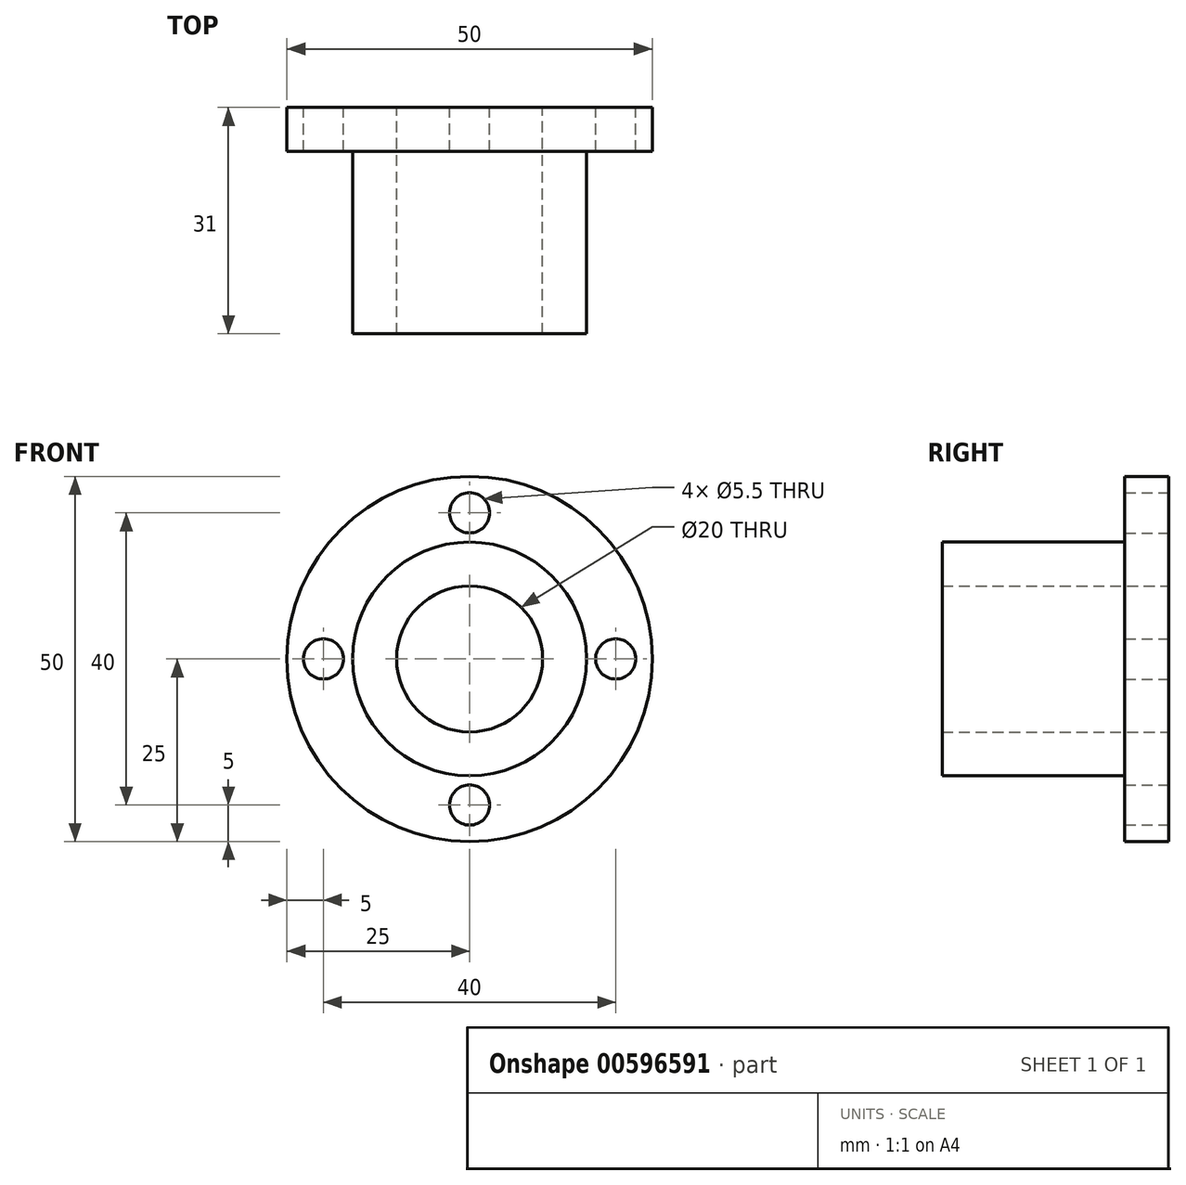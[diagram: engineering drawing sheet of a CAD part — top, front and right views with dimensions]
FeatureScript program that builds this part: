
annotation { "Feature Type Name" : "Feature", "Feature Type Description" : "" }
export const myFeature = defineFeature(function(context is Context, id is Id, definition is map)
    precondition{}
    {
        {
            var Q0;
            Q0=qCreatedBy(makeId("Front.planeOp"),FACE);
            var sketch = newSketch(context, id + "F0", { "sketchPlane" : qUnion([Q0])});
            skCircle(sketch, "E0", {"center": v(0, 0) * mm, "radius": 25 * mm});
            skSolve(sketch);
        }
        {
            var Q0;
            Q0 = qSketchRegion(id + "F0", true);
            extrude(context, id + "F1", {"entities" : qUnion([Q0]), "depth" : 6 * mm, "offsetDistance" : 25 * mm});
        }
        {
            var Q0;
            Q0=makeQuery(id+"F1.opExtrude","CAP_FACE",FACE,{"disambiguationData":[OSD([sQuery(id+"F0.wireOp",EDGE,"E0")])],"isStart":false});
            var sketch = newSketch(context, id + "F2", { "sketchPlane" : qUnion([Q0])});
            skCircle(sketch, "E1", {"center": v(0, 0) * mm, "radius": 16 * mm});
            skSolve(sketch);
        }
        {
            var Q0;
            Q0 = qSketchRegion(id + "F2", true);
            extrude(context, id + "F3", {"entities" : qUnion([Q0]), "operationType" : NewBodyOperationType.ADD, "depth" : 25 * mm, "offsetDistance" : 25 * mm});
        }
        {
            var Q0;
            Q0=makeQuery(id+"F1.opExtrude","CAP_FACE",FACE,{"disambiguationData":[OSD([sQuery(id+"F0.wireOp",EDGE,"E0")])],"isStart":true});
            var sketch = newSketch(context, id + "F4", { "sketchPlane" : qUnion([Q0])});
            skCircle(sketch, "E2", {"center": v(0, 0) * mm, "radius": 20 * mm, "construction": true});
            skCircle(sketch, "E3", {"center": v(0, 20) * mm, "radius": 2.75 * mm});
            skCircle(sketch, "E4.1.0", {"center": v(-20, 0) * mm, "radius": 2.75 * mm});
            skCircle(sketch, "E4.2.0", {"center": v(0, -20) * mm, "radius": 2.75 * mm});
            skCircle(sketch, "E4.3.0", {"center": v(20, 0) * mm, "radius": 2.75 * mm});
            skSolve(sketch);
        }
        {
            var Q0;
            Q0=makeQuery(id+"F4.imprint","IMPRINT",FACE,{"disambiguationData":[TD([[makeQuery(id+"F4.imprint","IMPRINT",EDGE,{"derivedFrom":sQuery(id+"F4.wireOp",EDGE,"E3")}),1.0]])]});
            var Q1;
            Q1=makeQuery(id+"F4.imprint","IMPRINT",FACE,{"disambiguationData":[TD([[makeQuery(id+"F4.imprint","IMPRINT",EDGE,{"derivedFrom":sQuery(id+"F4.wireOp",EDGE,"E4.1.0")}),1.0]])]});
            var Q2;
            Q2=makeQuery(id+"F4.imprint","IMPRINT",FACE,{"disambiguationData":[TD([[makeQuery(id+"F4.imprint","IMPRINT",EDGE,{"derivedFrom":sQuery(id+"F4.wireOp",EDGE,"E4.3.0")}),1.0]])]});
            var Q3;
            Q3=makeQuery(id+"F4.imprint","IMPRINT",FACE,{"disambiguationData":[TD([[makeQuery(id+"F4.imprint","IMPRINT",EDGE,{"derivedFrom":sQuery(id+"F4.wireOp",EDGE,"E4.2.0")}),1.0]])]});
            extrude(context, id + "F5", {"entities" : qUnion([Q0, Q1, Q2, Q3]), "operationType" : NewBodyOperationType.REMOVE, "endBound" : BoundingType.THROUGH_ALL, "oppositeDirection" : true, "depth" : 25 * mm, "offsetDistance" : 25 * mm});
        }
        {
            var Q0;
            Q0=makeQuery(id+"F1.opExtrude","CAP_FACE",FACE,{"disambiguationData":[OSD([sQuery(id+"F0.wireOp",EDGE,"E0")])],"isStart":true});
            var sketch = newSketch(context, id + "F6", { "sketchPlane" : qUnion([Q0])});
            skPoint(sketch, "E5", {"position": v(0, 0) * mm});
            skSolve(sketch);
        }
        {
            var Q0;
            Q0=sQuery(id+"F6.wireOp",VERTEX,"E5");
            var Q1;
            Q1=makeQuery(id+"F1.opExtrude","SWEPT_BODY",BODY,{"disambiguationData":[OSD([sQuery(id+"F0.wireOp",EDGE,"E0")])]});
            hole(context, id + "F7", {"style" : HoleStyle.SIMPLE, "endStyle" : HoleEndStyle.THROUGH, "holeDiameter" : 20 * mm, "majorDiameter" : 5 * mm, "isTappedThrough" : true, "tappedDepth" : 12 * mm, "tapClearance" : 3, "startFromSketch" : true, "locations" : qUnion([Q0]), "scope" : qUnion([Q1])});
        }
    });
